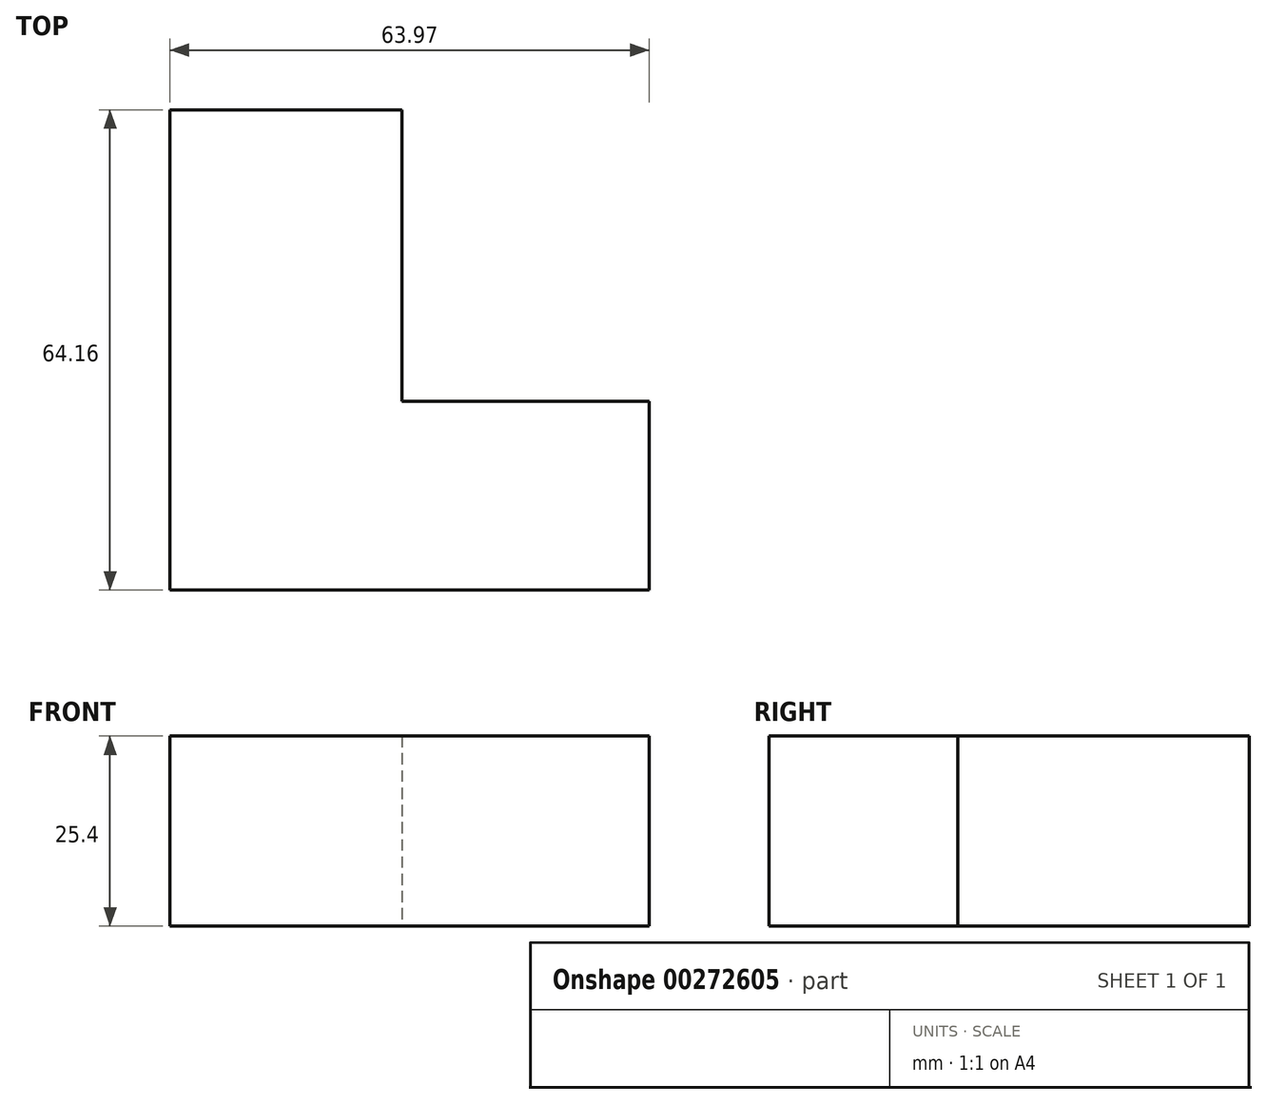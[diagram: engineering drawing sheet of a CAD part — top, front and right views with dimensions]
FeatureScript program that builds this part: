
annotation { "Feature Type Name" : "Feature", "Feature Type Description" : "" }
export const myFeature = defineFeature(function(context is Context, id is Id, definition is map)
    precondition{}
    {
        {
            var Q0;
            Q0=qCreatedBy(makeId("Top.planeOp"),FACE);
            var sketch = newSketch(context, id + "F0", { "sketchPlane" : qUnion([Q0])});
            skLineSegment(sketch, "E0", {"start": v(0, 0) * mm, "end": v(-63.97, 0) * mm});
            skLineSegment(sketch, "E1", {"start": v(-63.97, 0) * mm, "end": v(-63.97, 64.16) * mm});
            skLineSegment(sketch, "E2", {"start": v(-63.97, 64.16) * mm, "end": v(-33.04, 64.16) * mm});
            skLineSegment(sketch, "E3", {"start": v(-33.04, 64.16) * mm, "end": v(-33.04, 25.2) * mm});
            skLineSegment(sketch, "E4", {"start": v(-33.04, 25.2) * mm, "end": v(0, 25.2) * mm});
            skLineSegment(sketch, "E5", {"start": v(0, 25.2) * mm, "end": v(0, 0) * mm});
            skSolve(sketch);
        }
        {
            var Q0;
            Q0=makeQuery(id+"F0.imprint","IMPRINT",FACE,{"disambiguationData":[TD([[makeQuery(id+"F0.imprint","IMPRINT",EDGE,{"derivedFrom":sQuery(id+"F0.wireOp",EDGE,"E0")}),-1.0]])]});
            extrude(context, id + "F1", {"entities" : qUnion([Q0]), "depth" : 25.4 * mm});
        }
    });
